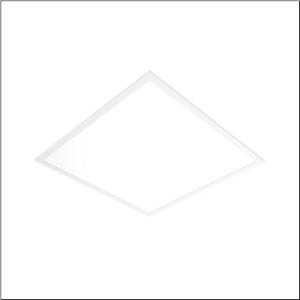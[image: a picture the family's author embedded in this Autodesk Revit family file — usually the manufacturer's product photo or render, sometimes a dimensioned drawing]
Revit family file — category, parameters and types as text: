
# Revit family: apollon_r__41_51mh12wd2422_e36b
name_source: partatom
category: Lighting Fixtures
units: mm (PartAtom-declared; Revit-internal decimal feet)

## family parameters
Cut with Voids When Loaded = No
Host = Face
Light Source = No
Part Type = Normal
Room Calculation Point = No
Round Connector Dimension = Use Diameter
Shared = No

## types (1)
- Apollon® 41 (1 x LED, 3700 lm, 35 W, 4000K)
    Apparent Load = 35 VA
    CIE Flux Codes = 63 87 97 100 100
    Color Rendering = 80
    Color Temperature = 4000K
    Default Elevation = 1800 mm
    Description = Apollon® 41, office luminaire, primary optical cover: prismatic diffuser, of PS, light emission: direct distribution, primary light characteristic: symmetric, installation type: lay-in mounting, LED, rated luminous flux: 3.700lm, luminous efficacy: 105lm/W, light colour: 840, colour temperature: 4000K, control gear: ECG DALI, with terminal, 5-pole, mains connection: 220..240V, AC, 50/60Hz, rated input power: 35W, housing, of aluminium section, traffic white (RAL 9016), module: M600, length: 595mm, width: 595mm, height: 32mm, housing upper side, of sheet steel, protection rating (complete): IP20, protection rating (lamp compartment, on room side): IP40, insulation class (complete): insulation class II (safety insulation), certification: CE, ENEC, permissible operating ambient temperature: -20..+40°C, packaging unit: 1 piece
    Height = 0 mm  [stored 0 ft]
    Lamp = 1 x LED
    Lamp Light Flux = 3700 lm
    Lamp Power = 35 W
    Lamp count = 1
    Length = 596 mm
    Luminous efficacy = 106 lm/W
    Manufacturer = Siteco
    ModVariant = No
    Model = 51MH12WD2422
    Mounting Place = Ceiling
    Mounting Type = Recessed
    Number of Poles = 1
    OnlyDefault = Yes
    Power Factor = 1
    Product Name = Apollon® 41
    Product group = office luminaire | ceiling recessed
    ProductGroupID = 401
    Protection Class = Protection class II
    Protection Degree = IP 20
    RLX_Detail_Level = 1
    RLX_Emergency_Light_Flux = 0 lm
    RLX_Emergency_Type = 0
    RLX_Emergency_Type_DB = No
    RlxData = <blob elided: 14885 chars, md5=6f8470b8>
    Socket = socket
    Standby Power = 0 W
    System Light Flux = 3700 lm
    System Power = 35 W
    Type Comments = Product without accessories
    Type Image = l_1291024.jpg
    URL = http://relux.com
    VarID = ---
    Voltage = 0 V
    Weight = 0.00 kg
    Width = 596 mm

note: [stored X ft] marks values corroborated as IEEE doubles in the binary element streams (Revit-internal decimal feet)

## geometry (parser evidence)
native form markers: Sweep x11
no freeform markers — native parametric forms only
